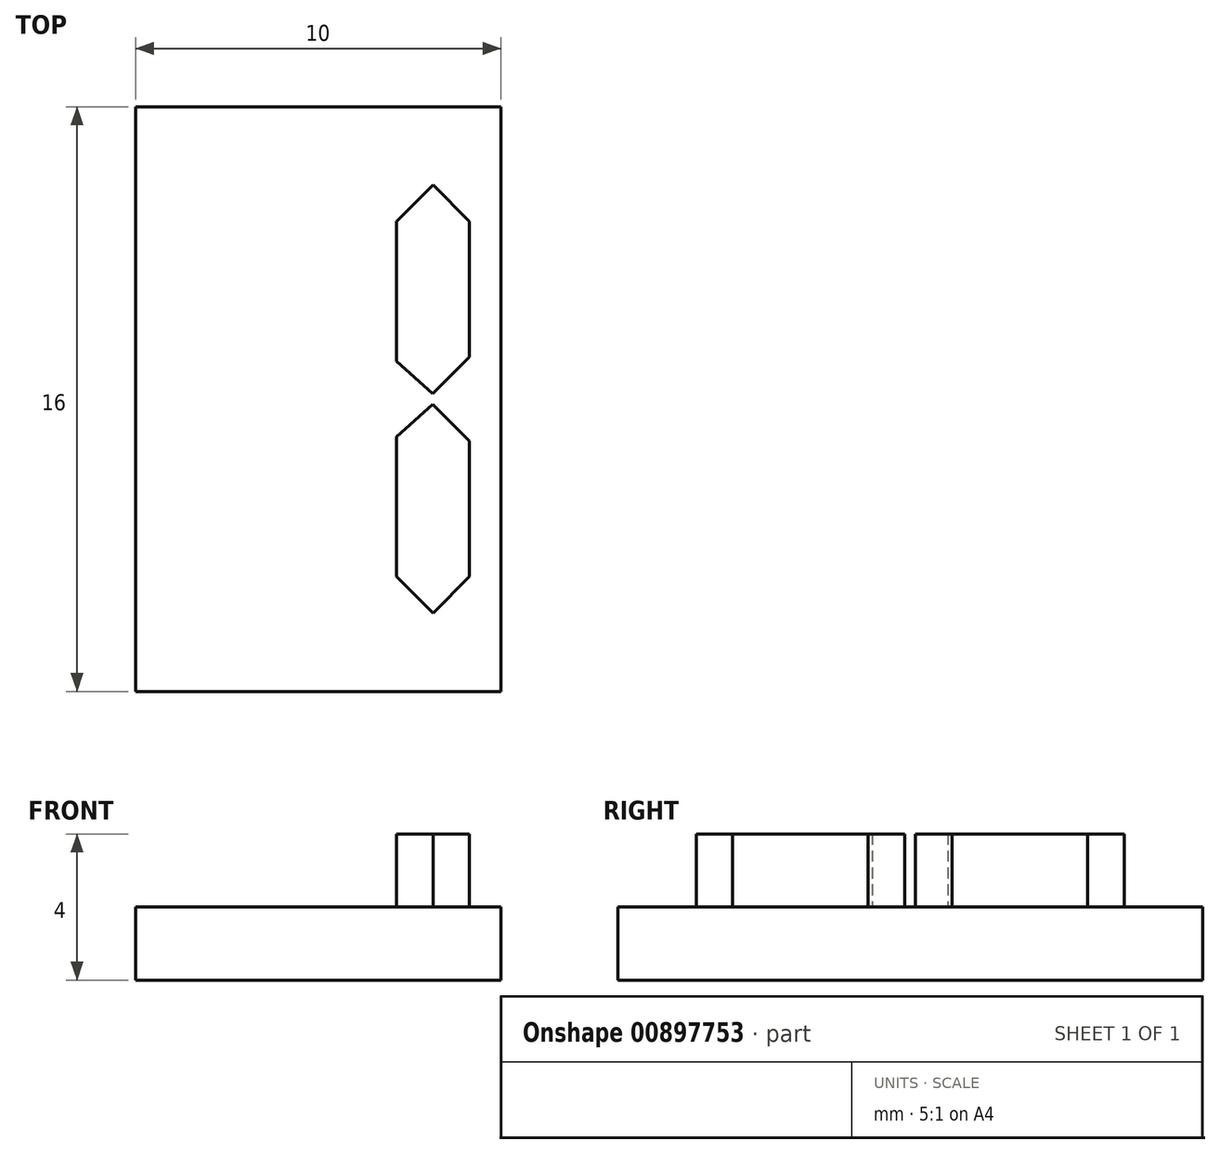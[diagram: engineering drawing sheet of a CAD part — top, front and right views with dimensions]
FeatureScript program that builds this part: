
annotation { "Feature Type Name" : "Feature", "Feature Type Description" : "" }
export const myFeature = defineFeature(function(context is Context, id is Id, definition is map)
    precondition{}
    {
        {
            var Q0;
            Q0=qCreatedBy(makeId("Top.planeOp"),FACE);
            var sketch = newSketch(context, id + "F0", { "sketchPlane" : qUnion([Q0])});
            skLineSegment(sketch, "E0.bottom", {"start": v(5, -8) * mm, "end": v(-5, -8) * mm});
            skLineSegment(sketch, "E0.top", {"start": v(5, 8) * mm, "end": v(-5, 8) * mm});
            skLineSegment(sketch, "E0.left", {"start": v(5, -8) * mm, "end": v(5, 8) * mm});
            skLineSegment(sketch, "E0.right", {"start": v(-5, -8) * mm, "end": v(-5, 8) * mm});
            skPoint(sketch, "E0.middle", {"position": v(0, 0) * mm});
            skSolve(sketch);
        }
        {
            var Q0;
            Q0=makeQuery(id+"F0.imprint","IMPRINT",FACE,{"disambiguationData":[TD([[makeQuery(id+"F0.imprint","IMPRINT",EDGE,{"derivedFrom":sQuery(id+"F0.wireOp",EDGE,"E0.bottom")}),-1.0]])]});
            extrude(context, id + "F1", {"entities" : qUnion([Q0]), "depth" : 2 * mm, "offsetDistance" : 25 * mm});
        }
        {
            var Q0;
            Q0=makeQuery(id+"F1.opExtrude","CAP_FACE",FACE,{"disambiguationData":[OSD([sQuery(id+"F0.wireOp",EDGE,"E0.bottom"),sQuery(id+"F0.wireOp",EDGE,"E0.top"),sQuery(id+"F0.wireOp",EDGE,"E0.left"),sQuery(id+"F0.wireOp",EDGE,"E0.right")])],"isStart":false});
            var sketch = newSketch(context, id + "F2", { "sketchPlane" : qUnion([Q0])});
            skLineSegment(sketch, "E1", {"start": v(-3, 8) * mm, "end": v(-3, -8) * mm, "construction": true});
            skLineSegment(sketch, "E2.0.1.0", {"start": v(-5, 6) * mm, "end": v(5, 6) * mm, "construction": true});
            skLineSegment(sketch, "E2.direction2", {"start": v(-5, 7) * mm, "end": v(-5, 6) * mm, "construction": true});
            skLineSegment(sketch, "E3.1.0.0", {"start": v(-2, 8) * mm, "end": v(-2, -8) * mm, "construction": true});
            skLineSegment(sketch, "E3.3.0.0", {"start": v(0, 8) * mm, "end": v(0, -8) * mm, "construction": true});
            skLineSegment(sketch, "E3.direction1", {"start": v(-3, -8) * mm, "end": v(-2, -8) * mm, "construction": true});
            skLineSegment(sketch, "E4", {"start": v(-2, 7) * mm, "end": v(-3, 6) * mm, "construction": true});
            skLineSegment(sketch, "E5", {"start": v(-3, 6) * mm, "end": v(-2, 5) * mm, "construction": true});
            skLineSegment(sketch, "E6", {"start": v(-2, 5) * mm, "end": v(0, 5) * mm, "construction": true});
            skLineSegment(sketch, "E7", {"start": v(-2, 7) * mm, "end": v(0, 7) * mm, "construction": true});
            skLineSegment(sketch, "E8.0", {"start": v(-3.14, 5.86) * mm, "end": v(-2.14, 4.86) * mm, "construction": true});
            skLineSegment(sketch, "E9", {"start": v(-2.14, 4.86) * mm, "end": v(-2.14, 1.03) * mm, "construction": true});
            skLineSegment(sketch, "E10.0", {"start": v(-4.14, 4.86) * mm, "end": v(-4.14, 1.15) * mm, "construction": true});
            skLineSegment(sketch, "E11", {"start": v(-3.14, 5.86) * mm, "end": v(-4.14, 4.86) * mm, "construction": true});
            skLineSegment(sketch, "E12", {"start": v(-4.14, 4.86) * mm, "end": v(5, 4.86) * mm, "construction": true});
            skLineSegment(sketch, "E13", {"start": v(0, 0.9) * mm, "end": v(-2, 0.9) * mm, "construction": true});
            skLineSegment(sketch, "E14", {"start": v(-2, 0.9) * mm, "end": v(-3, 0) * mm, "construction": true});
            skLineSegment(sketch, "E15.0", {"start": v(-2.14, 1.03) * mm, "end": v(-3.14, 0.15) * mm, "construction": true});
            skLineSegment(sketch, "E16", {"start": v(-3.14, 5.86) * mm, "end": v(-3.14, 0.15) * mm, "construction": true});
            skLineSegment(sketch, "E17", {"start": v(-4.14, 1.15) * mm, "end": v(-3.14, 0.15) * mm, "construction": true});
            skLineSegment(sketch, "E18.MirrorCS", {"start": v(0, -0.9) * mm, "end": v(-2, -0.9) * mm, "construction": true});
            skLineSegment(sketch, "E19.MirrorCS", {"start": v(-2, -0.9) * mm, "end": v(-3, 0) * mm, "construction": true});
            skLineSegment(sketch, "E20.MirrorCS", {"start": v(-2, -5) * mm, "end": v(0, -5) * mm, "construction": true});
            skLineSegment(sketch, "E21.MirrorCS", {"start": v(-3, -6) * mm, "end": v(-2, -5) * mm, "construction": true});
            skLineSegment(sketch, "E22.MirrorCS", {"start": v(-2, -7) * mm, "end": v(-3, -6) * mm, "construction": true});
            skLineSegment(sketch, "E23.MirrorCS", {"start": v(-2, -7) * mm, "end": v(0, -7) * mm, "construction": true});
            skLineSegment(sketch, "E24.MirrorCS", {"start": v(-3.14, -5.86) * mm, "end": v(-2.14, -4.86) * mm, "construction": true});
            skLineSegment(sketch, "E25.MirrorCS", {"start": v(-3.14, -5.86) * mm, "end": v(-4.14, -4.86) * mm, "construction": true});
            skLineSegment(sketch, "E26.MirrorCS", {"start": v(-4.14, -4.86) * mm, "end": v(-4.14, -1.15) * mm, "construction": true});
            skLineSegment(sketch, "E27.MirrorCS", {"start": v(-4.14, -1.15) * mm, "end": v(-3.14, -0.15) * mm, "construction": true});
            skLineSegment(sketch, "E28.MirrorCS", {"start": v(-2.14, -4.86) * mm, "end": v(-2.14, -1.03) * mm, "construction": true});
            skLineSegment(sketch, "E29.MirrorCS", {"start": v(-2.14, -1.03) * mm, "end": v(-3.14, -0.15) * mm, "construction": true});
            skLineSegment(sketch, "E30.MirrorCS", {"start": v(2, 7) * mm, "end": v(0, 7) * mm, "construction": true});
            skLineSegment(sketch, "E31.MirrorCS", {"start": v(2, 7) * mm, "end": v(3, 6) * mm, "construction": true});
            skLineSegment(sketch, "E32.MirrorCS", {"start": v(3, 6) * mm, "end": v(2, 5) * mm, "construction": true});
            skLineSegment(sketch, "E33.MirrorCS", {"start": v(2, 5) * mm, "end": v(0, 5) * mm, "construction": true});
            skLineSegment(sketch, "E34.MirrorCS", {"start": v(3.14, 5.86) * mm, "end": v(2.14, 4.86) * mm});
            skLineSegment(sketch, "E35.MirrorCS", {"start": v(3.14, 5.86) * mm, "end": v(4.14, 4.86) * mm});
            skLineSegment(sketch, "E36.MirrorCS", {"start": v(4.14, 4.86) * mm, "end": v(4.14, 1.15) * mm});
            skLineSegment(sketch, "E37.MirrorCS", {"start": v(4.14, 1.15) * mm, "end": v(3.14, 0.15) * mm});
            skLineSegment(sketch, "E38.MirrorCS", {"start": v(2.14, 4.86) * mm, "end": v(2.14, 1.03) * mm});
            skLineSegment(sketch, "E39.MirrorCS", {"start": v(2.14, 1.03) * mm, "end": v(3.14, 0.15) * mm});
            skLineSegment(sketch, "E40.MirrorCS", {"start": v(2, 0.9) * mm, "end": v(3, 0) * mm, "construction": true});
            skLineSegment(sketch, "E41.MirrorCS", {"start": v(0, 0.9) * mm, "end": v(2, 0.9) * mm, "construction": true});
            skLineSegment(sketch, "E42.MirrorCS", {"start": v(2, -0.9) * mm, "end": v(3, 0) * mm, "construction": true});
            skLineSegment(sketch, "E43.MirrorCS", {"start": v(0, -0.9) * mm, "end": v(2, -0.9) * mm, "construction": true});
            skLineSegment(sketch, "E44.MirrorCS", {"start": v(2.14, -1.03) * mm, "end": v(3.14, -0.15) * mm});
            skLineSegment(sketch, "E45.MirrorCS", {"start": v(4.14, -1.15) * mm, "end": v(3.14, -0.15) * mm});
            skLineSegment(sketch, "E46.MirrorCS", {"start": v(4.14, -4.86) * mm, "end": v(4.14, -1.15) * mm});
            skLineSegment(sketch, "E47.MirrorCS", {"start": v(2.14, -4.86) * mm, "end": v(2.14, -1.03) * mm});
            skLineSegment(sketch, "E48.MirrorCS", {"start": v(3.14, -5.86) * mm, "end": v(2.14, -4.86) * mm});
            skLineSegment(sketch, "E49.MirrorCS", {"start": v(3.14, -5.86) * mm, "end": v(4.14, -4.86) * mm});
            skLineSegment(sketch, "E50.MirrorCS", {"start": v(3, -6) * mm, "end": v(2, -5) * mm, "construction": true});
            skLineSegment(sketch, "E51.MirrorCS", {"start": v(2, -5) * mm, "end": v(0, -5) * mm, "construction": true});
            skLineSegment(sketch, "E52.MirrorCS", {"start": v(2, -7) * mm, "end": v(3, -6) * mm, "construction": true});
            skLineSegment(sketch, "E53.MirrorCS", {"start": v(2, -7) * mm, "end": v(0, -7) * mm, "construction": true});
            skSolve(sketch);
        }
        {
            var Q0;
            Q0=qSketchRegion(id+"F2",true);
            extrude(context, id + "F3", {"entities" : qUnion([Q0]), "operationType" : NewBodyOperationType.ADD, "depth" : 2 * mm, "offsetDistance" : 25 * mm});
        }
    });
